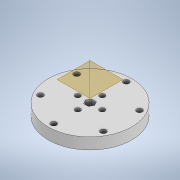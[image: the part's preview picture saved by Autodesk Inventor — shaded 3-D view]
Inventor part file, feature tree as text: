
AUTODESK INVENTOR PART (.ipt)
format: ipt  version: 2020 (Build 240168000, 168)  size: 151,040 bytes
history: native  units: in
note: dims shown in document units (in); Inventor stores cm internally (conversion verified against a paired STEP export)
features: extrude x4, sketch x4, plane x2, pattern_circular x2, other x1
ambient origin geometry x8: Origin, YZ Plane, XZ Plane, XY Plane, X Axis, Y Axis, Z Axis, Center Point
bodies: Solid1 (feature_tree)
feature tree (13):
  extrude  "Extrusion1"  Depth=0.3in TaperAngle=0.0deg
  plane  "Work Plane5"
  extrude  "Extrusion4"  Depth=1.0in TaperAngle=0.0deg
  extrude  "Extrusion5"  Depth=0.075in
  plane  "Work Plane6"
  other  "Work Axis1"
  pattern_circular  "Circular Pattern1"  Count=6 Angle=360.0deg
  extrude  "Extrusion6"  Depth=0.07in
  pattern_circular  "Circular Pattern2"  [2 undecoded]
  sketch  "Sketch1"  dims[d0=2.2in d1=0.3in d2=0.0in]
  sketch  "Sketch5"  dims[d10=0.105in d11=1.0in d12=0.0in]
  sketch  "Sketch6"  dims[d13=0.07in d14=0.075in]
  sketch  "Sketch8"  dims[d15=1.0in d16=0.0in d17=2.3622in d18=360.0deg d20=0.13in d21=0.07in d22=1.0in d23=0.0in d24=1.5748in d25=360.0deg d27=0.5in d28=0.0344in d29=0.5in d30=0.0344in]
note: 2 required parameter values undecoded (feature->parameter linkage not recoverable at this tier; creation-order binding heuristic only, values carry confidence <= 0.55)
